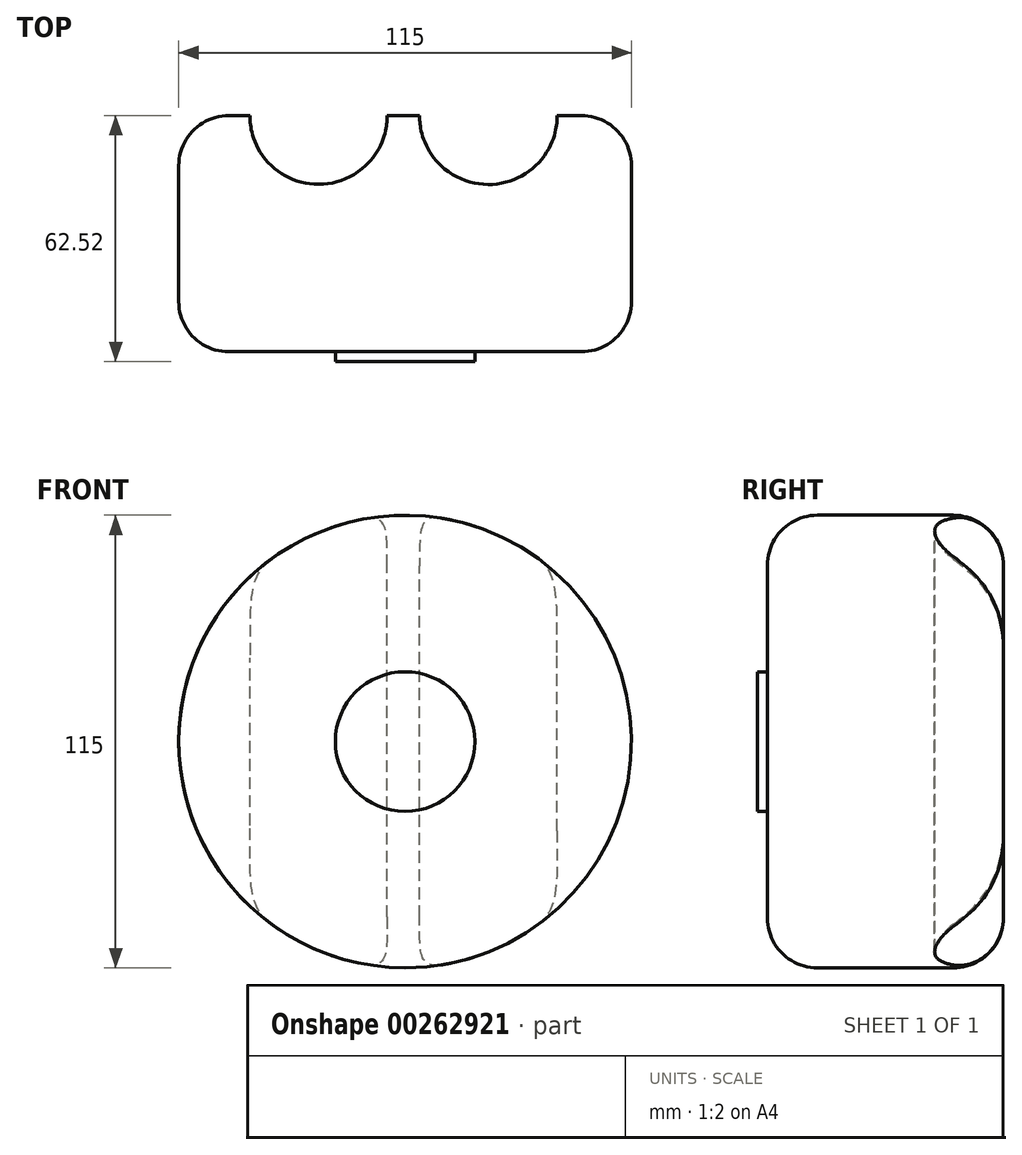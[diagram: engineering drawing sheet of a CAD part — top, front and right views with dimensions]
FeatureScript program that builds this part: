
annotation { "Feature Type Name" : "Feature", "Feature Type Description" : "" }
export const myFeature = defineFeature(function(context is Context, id is Id, definition is map)
    precondition{}
    {
        {
            var Q0;
            Q0=qCreatedBy(makeId("Front.planeOp"),FACE);
            var sketch = newSketch(context, id + "F0", { "sketchPlane" : qUnion([Q0])});
            skCircle(sketch, "E0", {"center": v(0, 0) * mm, "radius": 57.5 * mm});
            skSolve(sketch);
        }
        {
            var Q0;
            Q0 = qSketchRegion(id + "F0", true);
            var Q1;
            Q1=makeQuery(id+"F0.imprint","IMPRINT",FACE,{"disambiguationData":[TD([[makeQuery(id+"F0.imprint","IMPRINT",EDGE,{"derivedFrom":sQuery(id+"F0.wireOp",EDGE,"E0")}),1.0]])]});
            extrude(context, id + "F1", {"entities" : qUnion([Q0, Q1]), "depth" : 59.98 * mm});
        }
        {
            var Q0;
            Q0=makeQuery(id+"F1.opExtrude","CAP_EDGE",EDGE,{"disambiguationData":[OSD([sQuery(id+"F0.wireOp",EDGE,"E0")])],"isStart":false});
            fillet(context, id + "F2", {"entities" : qUnion([Q0]), "radius" : 12.7 * mm, "tangentPropagation" : true, "allowEdgeOverflow" : false});
        }
        {
            var Q0;
            Q0=makeQuery(id+"F1.opExtrude","CAP_FACE",FACE,{"disambiguationData":[OSD([sQuery(id+"F0.wireOp",EDGE,"E0")])],"isStart":true});
            fillet(context, id + "F3", {"entities" : qUnion([Q0]), "radius" : 12.7 * mm, "tangentPropagation" : true, "allowEdgeOverflow" : false});
        }
        {
            var Q0;
            Q0=makeQuery(id+"F1.opExtrude","CAP_FACE",FACE,{"disambiguationData":[OSD([sQuery(id+"F0.wireOp",EDGE,"E0")])],"isStart":false});
            var sketch = newSketch(context, id + "F4", { "sketchPlane" : qUnion([Q0])});
            skCircle(sketch, "E1", {"center": v(0, 0) * mm, "radius": 17.73 * mm});
            skSolve(sketch);
        }
        {
            var Q0;
            Q0=makeQuery(id+"F4.imprint","IMPRINT",FACE,{"disambiguationData":[TD([[makeQuery(id+"F4.imprint","IMPRINT",EDGE,{"derivedFrom":sQuery(id+"F4.wireOp",EDGE,"E1")}),1.0]])]});
            extrude(context, id + "F5", {"entities" : qUnion([Q0]), "operationType" : NewBodyOperationType.ADD, "depth" : 2.54 * mm});
        }
        {
            var Q0;
            Q0=qCreatedBy(makeId("Top.planeOp"),FACE);
            var sketch = newSketch(context, id + "F6", { "sketchPlane" : qUnion([Q0])});
            skCircle(sketch, "E2", {"center": v(21.16, 0) * mm, "radius": 17.49 * mm});
            skSolve(sketch);
        }
        {
            var Q0;
            Q0=qCreatedBy(makeId("Top.planeOp"),FACE);
            var sketch = newSketch(context, id + "F7", { "sketchPlane" : qUnion([Q0])});
            skCircle(sketch, "E3", {"center": v(-22, 0) * mm, "radius": 17.44 * mm});
            skSolve(sketch);
        }
        {
            var Q0;
            Q0=makeQuery(id+"F6.imprint","IMPRINT",FACE,{"disambiguationData":[TD([[makeQuery(id+"F6.imprint","IMPRINT",EDGE,{"derivedFrom":sQuery(id+"F6.wireOp",EDGE,"E2")}),1.0]])]});
            var Q1;
            Q1=sQuery(id+"F6.wireOp",EDGE,"E2");
            extrude(context, id + "F8", {"entities" : qUnion([Q0]), "operationType" : NewBodyOperationType.REMOVE, "surfaceEntities" : qUnion([Q1]), "oppositeDirection" : true, "depth" : 68.42 * mm});
        }
        {
            var Q0;
            Q0=makeQuery(id+"F7.imprint","IMPRINT",FACE,{"disambiguationData":[TD([[makeQuery(id+"F7.imprint","IMPRINT",EDGE,{"derivedFrom":sQuery(id+"F7.wireOp",EDGE,"E3")}),1.0]])]});
            var Q1;
            Q1=sQuery(id+"F7.wireOp",EDGE,"E3");
            extrude(context, id + "F9", {"entities" : qUnion([Q0]), "operationType" : NewBodyOperationType.REMOVE, "surfaceEntities" : qUnion([Q1]), "oppositeDirection" : true, "depth" : 79.7 * mm});
        }
        {
            var Q0;
            Q0=qCreatedBy(makeId("Right.planeOp"),FACE);
            var sketch = newSketch(context, id + "F10", { "sketchPlane" : qUnion([Q0])});
            skArc(sketch, "E4", {"start": v(-15.9, -62.6) * mm, "mid": v(-49.94, -40.95) * mm, "end": v(-64.5, -3.33) * mm});
            skSolve(sketch);
        }
        {
            var Q0;
            Q0=makeQuery(id+"F9.boolean.opBoolean","COPY",FACE,{"derivedFrom":makeQuery(id+"F9.opExtrude","CAP_FACE",FACE,{"disambiguationData":[OSD([sQuery(id+"F7.wireOp",EDGE,"E3")])],"isStart":true})});
            var Q1;
            Q1=makeQuery(id+"F8.boolean.opBoolean","COPY",FACE,{"derivedFrom":makeQuery(id+"F8.opExtrude","CAP_FACE",FACE,{"disambiguationData":[OSD([sQuery(id+"F6.wireOp",EDGE,"E2")])],"isStart":true})});
            var Q2;
            Q2=sQuery(id+"F10.wireOp",EDGE,"E4");
            extrude(context, id + "F11", {"entities" : qUnion([Q0, Q1]), "operationType" : NewBodyOperationType.REMOVE, "surfaceEntities" : qUnion([Q2]), "oppositeDirection" : true, "depth" : 109.13 * mm});
        }
    });
